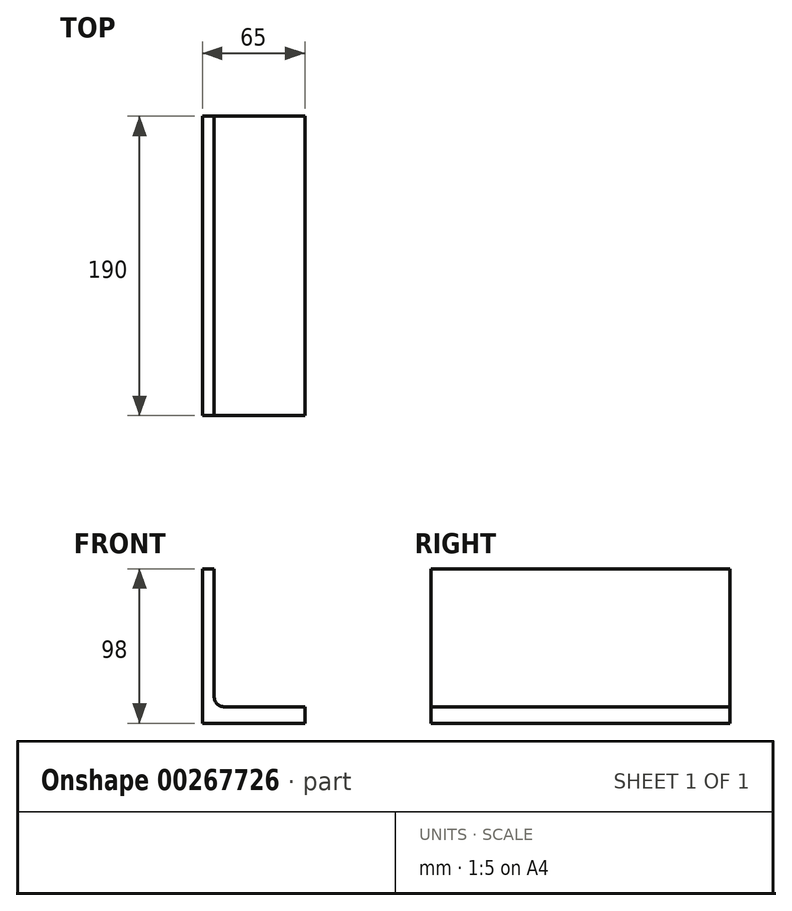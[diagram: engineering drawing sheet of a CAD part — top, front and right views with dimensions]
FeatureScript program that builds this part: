
annotation { "Feature Type Name" : "Feature", "Feature Type Description" : "" }
export const myFeature = defineFeature(function(context is Context, id is Id, definition is map)
    precondition{}
    {
        {
            var Q0;
            Q0=qCreatedBy(makeId("Front.planeOp"),FACE);
            var sketch = newSketch(context, id + "F0", { "sketchPlane" : qUnion([Q0])});
            skLineSegment(sketch, "E0.top", {"start": v(32.5, -80) * mm, "end": v(-32.5, -80) * mm});
            skLineSegment(sketch, "E0.right", {"start": v(-32.5, 18) * mm, "end": v(-32.5, -80) * mm});
            skPoint(sketch, "E0.middle", {"position": v(0, 0) * mm});
            skLineSegment(sketch, "E1.0", {"start": v(32.5, -69.5) * mm, "end": v(-19, -69.5) * mm});
            skLineSegment(sketch, "E2.0", {"start": v(-25, 18) * mm, "end": v(-25, -63.5) * mm});
            skArc(sketch, "E3.filletArc", {"start": v(-25, -63.5) * mm, "mid": v(-23.24, -67.74) * mm, "end": v(-19, -69.5) * mm});
            skLineSegment(sketch, "E4.trimOffspring", {"start": v(32.5, -69.5) * mm, "end": v(32.5, -80) * mm});
            skLineSegment(sketch, "E5", {"start": v(-32.5, 18) * mm, "end": v(-25, 18) * mm});
            skPoint(sketch, "E0.bottom.end.orphan", {"position": v(-32.5, 80) * mm});
            skPoint(sketch, "E0.left.start.orphan", {"position": v(32.5, 80) * mm});
            skSolve(sketch);
        }
        {
            var Q0;
            {var subQ3=sQuery(id+"F0.wireOp",EDGE,"E0.bottom");Q0=makeQuery(id+"F0.imprint","IMPRINT",FACE,{"disambiguationData":[TD([[makeQuery(id+"F0.imprint","IMPRINT",EDGE,{"derivedFrom":subQ3}),1.0]])]});}
            var Q1;
            Q1=makeQuery(id+"F0.imprint","IMPRINT",FACE,{"disambiguationData":[TD([[makeQuery(id+"F0.imprint","IMPRINT",EDGE,{"derivedFrom":sQuery(id+"F0.wireOp",EDGE,"E0.top")}),-1.0]])]});
            extrude(context, id + "F1", {"entities" : qUnion([Q0, Q1]), "oppositeDirection" : true, "depth" : 190 * mm});
        }
    });
